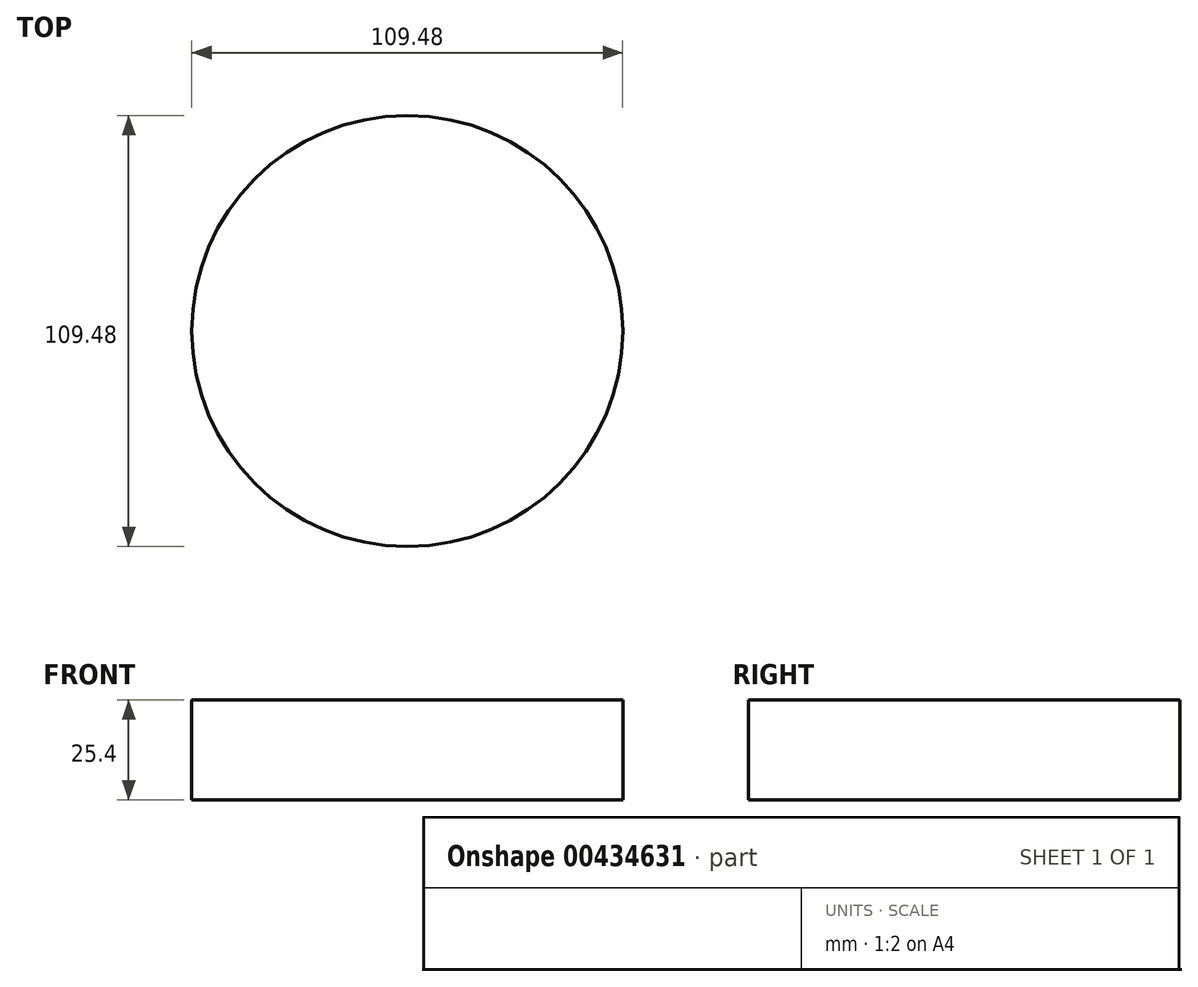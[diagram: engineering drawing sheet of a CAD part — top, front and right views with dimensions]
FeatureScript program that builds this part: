
annotation { "Feature Type Name" : "Feature", "Feature Type Description" : "" }
export const myFeature = defineFeature(function(context is Context, id is Id, definition is map)
    precondition{}
    {
        {
            var Q0;
            Q0=qCreatedBy(makeId("Top.planeOp"),FACE);
            var sketch = newSketch(context, id + "F0", { "sketchPlane" : qUnion([Q0])});
            skCircle(sketch, "E0", {"center": v(0, 0) * mm, "radius": 54.74 * mm});
            skSolve(sketch);
        }
        {
            var Q0;
            Q0=makeQuery(id+"F0.imprint","IMPRINT",FACE,{"disambiguationData":[TD([[makeQuery(id+"F0.imprint","IMPRINT",EDGE,{"derivedFrom":sQuery(id+"F0.wireOp",EDGE,"E0")}),1.0]])]});
            extrude(context, id + "F1", {"entities" : qUnion([Q0]), "depth" : 25.4 * mm});
        }
    });
